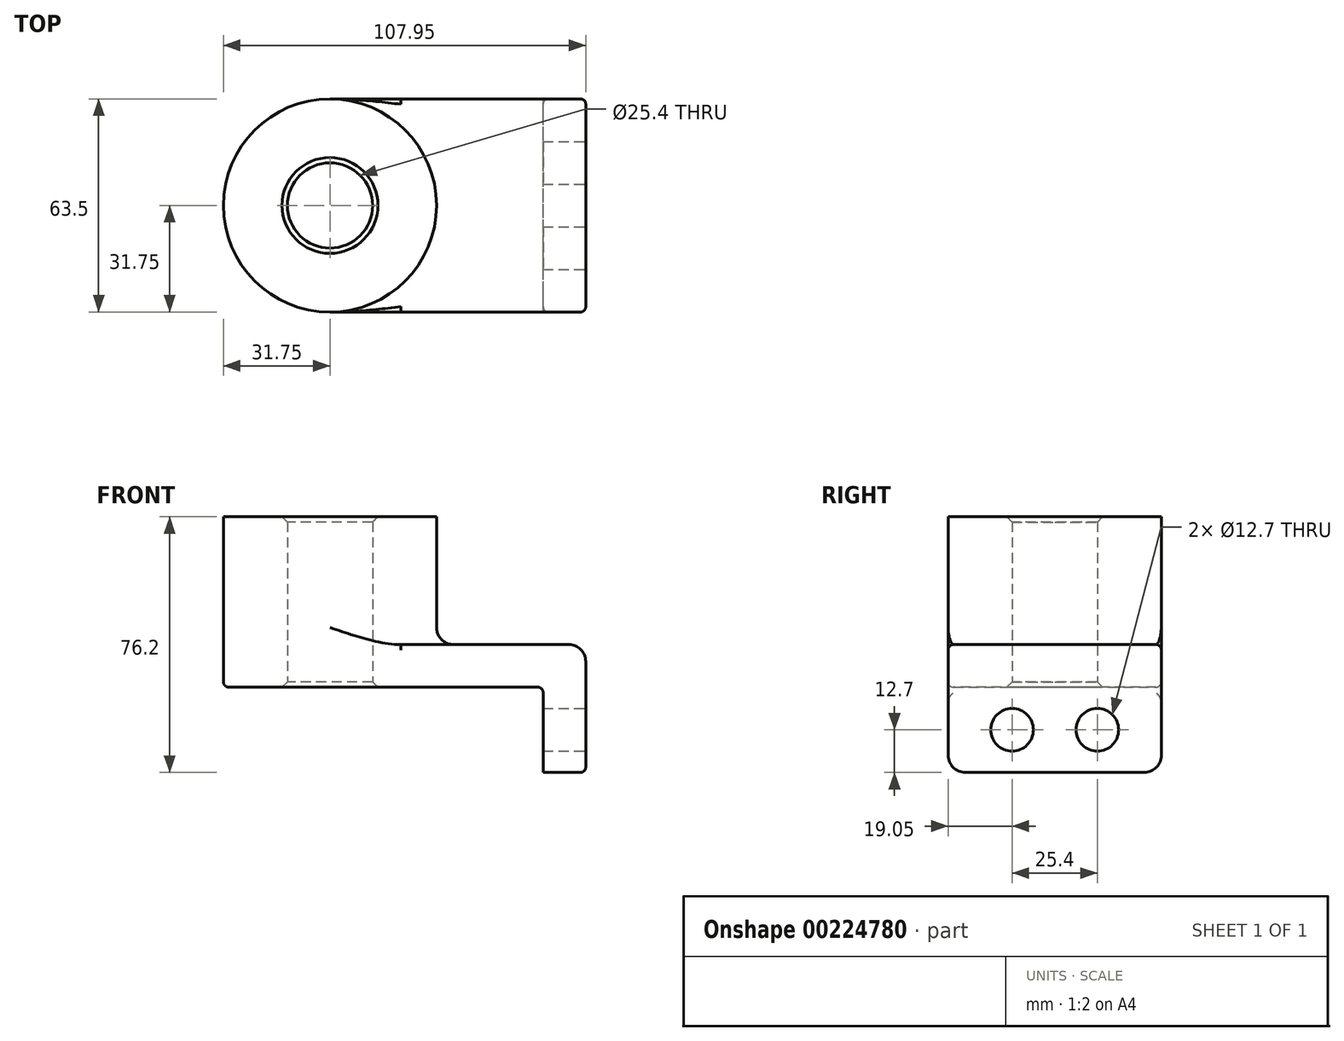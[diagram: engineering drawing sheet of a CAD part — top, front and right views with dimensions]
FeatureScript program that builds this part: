
annotation { "Feature Type Name" : "Feature", "Feature Type Description" : "" }
export const myFeature = defineFeature(function(context is Context, id is Id, definition is map)
    precondition{}
    {
        {
            var Q0;
            Q0=qCreatedBy(makeId("Top.planeOp"),FACE);
            var sketch = newSketch(context, id + "F0", { "sketchPlane" : qUnion([Q0])});
            skLineSegment(sketch, "E0.bottom", {"start": v(38.1, -31.75) * mm, "end": v(-38.1, -31.75) * mm});
            skLineSegment(sketch, "E0.top", {"start": v(38.1, 31.75) * mm, "end": v(-38.1, 31.75) * mm});
            skLineSegment(sketch, "E0.left", {"start": v(38.1, -31.75) * mm, "end": v(38.1, 31.75) * mm});
            skLineSegment(sketch, "E0.right", {"start": v(-38.1, -31.75) * mm, "end": v(-38.1, 31.75) * mm});
            skPoint(sketch, "E0.middle", {"position": v(0, 0) * mm});
            skCircle(sketch, "E1", {"center": v(-38.1, 0) * mm, "radius": 31.75 * mm});
            skCircle(sketch, "E2", {"center": v(-38.1, 0) * mm, "radius": 12.7 * mm});
            skSolve(sketch);
        }
        {
            var Q0;
            Q0 = qSketchRegion(id + "F0", true);
            extrude(context, id + "F1", {"entities" : qUnion([Q0]), "depth" : 12.7 * mm});
        }
        {
            var Q0;
            {var subQ1=sQuery(id+"F0.wireOp",EDGE,"E0.right");var subQ3=sQuery(id+"F0.wireOp",EDGE,"E2");var subQ4=makeQuery(id+"F0.imprint","INTERSECT",VERTEX,{"disambiguationData":[OD(0.0)],"derivedFrom":[subQ1,subQ3]});Q0=makeQuery(id+"F0.imprint","IMPRINT",FACE,{"disambiguationData":[TD([[makeQuery(id+"F0.imprint","IMPRINT",EDGE,{"disambiguationData":[TD([[subQ4,1.0]])],"derivedFrom":subQ3}),-1.0]])]});}
            var Q1;
            {var subQ1=sQuery(id+"F0.wireOp",EDGE,"E0.right");var subQ3=sQuery(id+"F0.wireOp",EDGE,"E2");var subQ4=makeQuery(id+"F0.imprint","INTERSECT",VERTEX,{"disambiguationData":[OD(0.0)],"derivedFrom":[subQ1,subQ3]});Q1=makeQuery(id+"F0.imprint","IMPRINT",FACE,{"disambiguationData":[TD([[makeQuery(id+"F0.imprint","IMPRINT",EDGE,{"disambiguationData":[TD([[subQ4,-1.0]])],"derivedFrom":subQ3}),-1.0]])]});}
            extrude(context, id + "F2", {"entities" : qUnion([Q0, Q1]), "operationType" : NewBodyOperationType.ADD, "depth" : 50.8 * mm});
        }
        {
            var Q0;
            Q0=makeQuery(id+"F1.opExtrude","SWEPT_FACE",FACE,{"disambiguationData":[OSD([sQuery(id+"F0.wireOp",EDGE,"E0.left")])]});
            var sketch = newSketch(context, id + "F3", { "sketchPlane" : qUnion([Q0])});
            skLineSegment(sketch, "E3.bottom", {"start": v(-31.75, 12.7) * mm, "end": v(31.75, 12.7) * mm});
            skLineSegment(sketch, "E3.top", {"start": v(-31.75, -25.4) * mm, "end": v(31.75, -25.4) * mm});
            skLineSegment(sketch, "E3.left", {"start": v(-31.75, 12.7) * mm, "end": v(-31.75, -25.4) * mm});
            skLineSegment(sketch, "E3.right", {"start": v(31.75, 12.7) * mm, "end": v(31.75, -25.4) * mm});
            skCircle(sketch, "E4", {"center": v(-12.7, -12.7) * mm, "radius": 6.35 * mm});
            skLineSegment(sketch, "E5", {"start": v(0, 0) * mm, "end": v(0, -25.4) * mm});
            skCircle(sketch, "E6.MirrorC", {"center": v(12.7, -12.7) * mm, "radius": 6.35 * mm});
            skSolve(sketch);
        }
        {
            var Q0;
            Q0 = qSketchRegion(id + "F3", true);
            extrude(context, id + "F4", {"entities" : qUnion([Q0]), "operationType" : NewBodyOperationType.ADD, "oppositeDirection" : true, "depth" : 12.7 * mm});
        }
        {
            var Q0;
            {var subQ0=sQuery(id+"F0.wireOp",EDGE,"E1");Q0=makeQuery(id+"F2.boolean.opBoolean","INTERSECT",EDGE,{"derivedFrom":[makeQuery(id+"F1.opExtrude","CAP_FACE",FACE,{"disambiguationData":[OSD([sQuery(id+"F0.wireOp",EDGE,"E0.bottom"),sQuery(id+"F0.wireOp",EDGE,"E0.top"),sQuery(id+"F0.wireOp",EDGE,"E0.left"),subQ0,sQuery(id+"F0.wireOp",EDGE,"E2")])],"isStart":false}),makeQuery(id+"F2.opExtrude","SWEPT_FACE",FACE,{"disambiguationData":[OSD([subQ0])]})]});}
            var Q1;
            Q1=makeQuery(id+"F1.opExtrude","CAP_EDGE",EDGE,{"disambiguationData":[OSD([sQuery(id+"F0.wireOp",EDGE,"E0.left")])],"isStart":false});
            var Q2;
            Q2=makeQuery(id+"F4.opExtrude","SWEPT_EDGE",EDGE,{"disambiguationData":[OSD([sQuery(id+"F3.wireOp",EDGE,"E3.top"),sQuery(id+"F3.wireOp",EDGE,"E3.left")])]});
            var Q3;
            Q3=makeQuery(id+"F4.opExtrude","SWEPT_EDGE",EDGE,{"disambiguationData":[OSD([sQuery(id+"F3.wireOp",EDGE,"E3.top"),sQuery(id+"F3.wireOp",EDGE,"E3.right")])]});
            fillet(context, id + "F5", {"entities" : qUnion([Q0, Q1, Q2, Q3]), "radius" : 5.08 * mm, "tangentPropagation" : true, "allowEdgeOverflow" : false});
        }
        {
            var Q0;
            Q0=makeQuery(id+"F1.opExtrude","CAP_EDGE",EDGE,{"disambiguationData":[OSD([sQuery(id+"F0.wireOp",EDGE,"E0.bottom")])],"isStart":false});
            var Q1;
            Q1=makeQuery(id+"F1.opExtrude","CAP_EDGE",EDGE,{"disambiguationData":[OSD([sQuery(id+"F0.wireOp",EDGE,"E0.bottom")])],"isStart":true});
            var Q2;
            Q2=makeQuery(id+"F4.boolean.opBoolean","INTERSECT",EDGE,{"derivedFrom":[makeQuery(id+"F1.opExtrude","CAP_FACE",FACE,{"disambiguationData":[OSD([sQuery(id+"F0.wireOp",EDGE,"E0.bottom"),sQuery(id+"F0.wireOp",EDGE,"E0.top"),sQuery(id+"F0.wireOp",EDGE,"E0.left"),sQuery(id+"F0.wireOp",EDGE,"E1"),sQuery(id+"F0.wireOp",EDGE,"E2")])],"isStart":true}),makeQuery(id+"F4.opExtrude","CAP_FACE",FACE,{"disambiguationData":[OSD([sQuery(id+"F3.wireOp",EDGE,"E3.bottom"),sQuery(id+"F3.wireOp",EDGE,"E3.top"),sQuery(id+"F3.wireOp",EDGE,"E3.left"),sQuery(id+"F3.wireOp",EDGE,"E3.right"),sQuery(id+"F3.wireOp",EDGE,"E4"),sQuery(id+"F3.wireOp",EDGE,"E6.MirrorC")])],"isStart":false})]});
            fillet(context, id + "F6", {"entities" : qUnion([Q0, Q1, Q2]), "radius" : 1.59 * mm, "tangentPropagation" : true, "allowEdgeOverflow" : false});
        }
        {
            var Q0;
            {var subQ0=sQuery(id+"F0.wireOp",EDGE,"E2");Q0=makeQuery(id+"F2.boolean.opBoolean","MERGE",FACE,{"derivedFrom":[makeQuery(id+"F1.opExtrude","SWEPT_FACE",FACE,{"disambiguationData":[OSD([subQ0])]}),makeQuery(id+"F2.opExtrude","SWEPT_FACE",FACE,{"disambiguationData":[OSD([subQ0])]})]});}
            chamfer(context, id + "F7", {"entities" : qUnion([Q0]), "width" : 1.59 * mm, "tangentPropagation" : true});
        }
    });
